# Revit family: Table-Teknion-JNHTRF-Navigate_Height_Adjustable_Rectangular-2018
name_source: partatom
category: Furniture
revit_build: Autodesk Revit 2018 (Build: 20190510_1515(x64)
units: mm (PartAtom-declared; Revit-internal decimal feet)

## family parameters
Always vertical = Yes
Cut with Voids When Loaded = No
OmniClass Number = 23.40.20.00
OmniClass Title = General Furniture and Specialties
Room Calculation Point = No
Shared = Yes
Work Plane-Based = No

## types (4) — shared parameters
Assembly Code = E2020200
Manufacturer = Teknion
Manufacturer Fax = 416.661.4586
Part Number = JNHTRF
Product Documentation Link = https://www.teknion.com
Product Documentation Link 2 = https://www.teknion.com
Product Line = Expansion Cityline
Product Page URL = https://www.teknion.com
Series = Expansion Cityline
Sustainability Data = https://www.teknion.com
URL = www.teknion.com
Unit Weight URL = http://www.teknion.com
Warranty = http://www.teknion.com

## per-type parameters (varying)
| type | CC | Depth | Description | Frame Offset | Model | S | TT | U |
| T-Legs, User Optimized Width Configuration | No | 29 " | Navigate Height-Adjustable Base - Rectangular, Navigate Leg Style, T-Legs Application, 29 Depth, Urser Optimized Width Configuration | 15.011 " | JNHTRFNTT_29_U | No | Yes | Yes |
| T-Legs, Standard Width Configuration | No | 29 " | Navigate Height-Adjustable Base - Rectangular, Navigate Leg Style, T-Legs Application, 29 Depth, Standard Width Configuration | 15.011 " | JNHTRFNTT_29_S | Yes | Yes | No |
| C-Legs, Standard Width Configuration | Yes | 23 " | Navigate Height-Adjustable Base - Rectangular, Navigate Leg Style, C-Legs Application, 29 Depth, Standard Width Configuration | 10 " | JNHTRFNCC_29_S | Yes | No | No |
| C-Legs, User Optimized Width Configuration | Yes | 23 " | Navigate Height-Adjustable Base - Rectangular, Navigate Leg Style, C-Legs Application, 29 Depth, User Optimzed Width Configuration | 10 " | JNHTRFNCC_29_U | No | No | Yes |

## geometry (parser evidence)
native form markers: Sweep x2
no freeform markers — native parametric forms only
